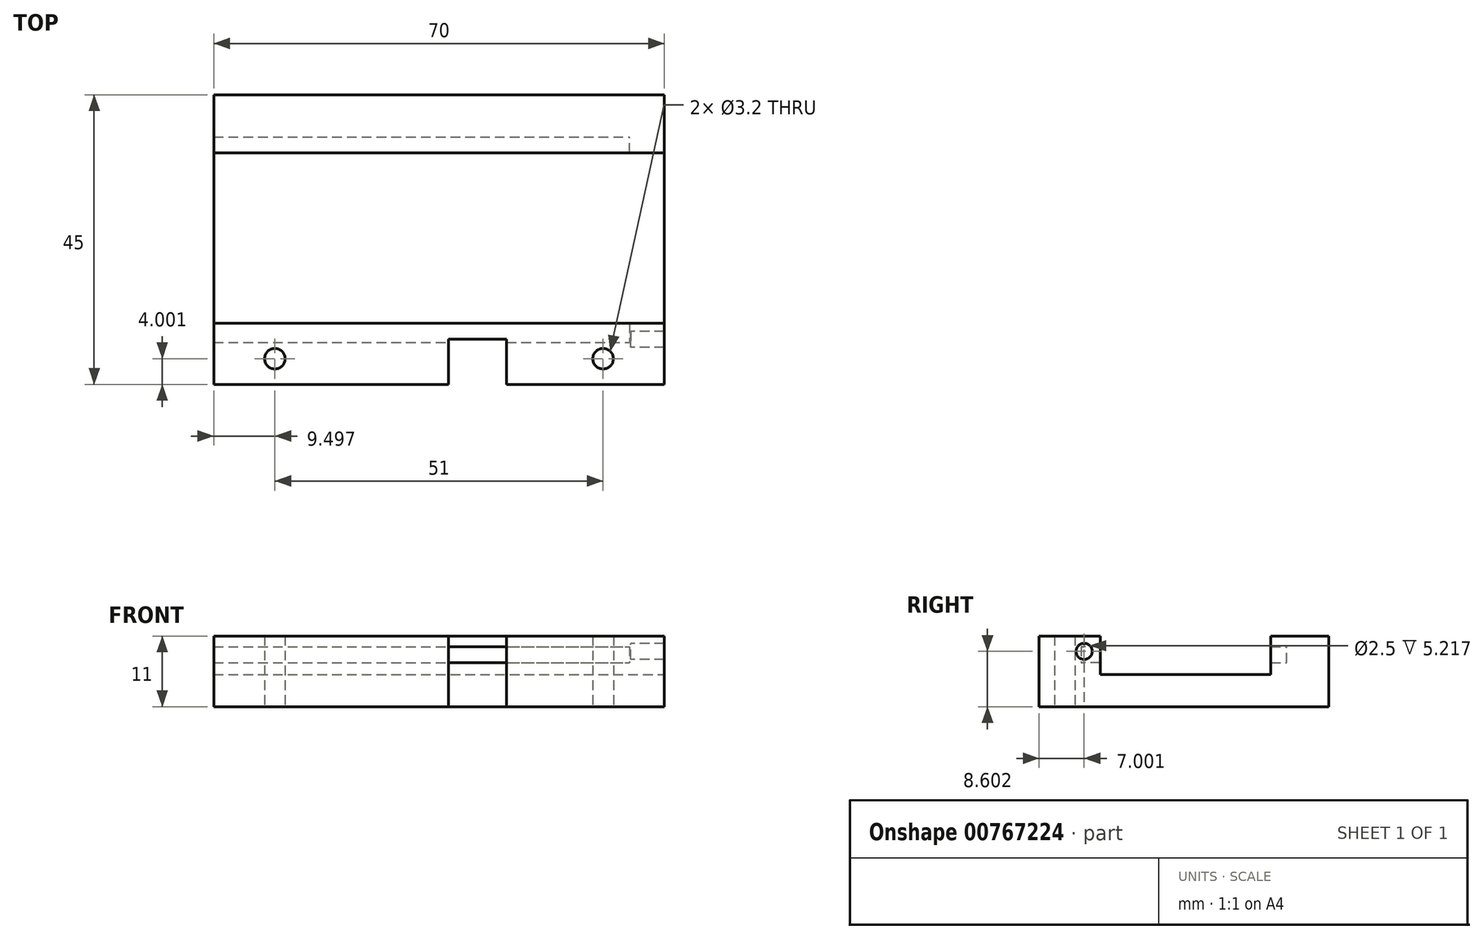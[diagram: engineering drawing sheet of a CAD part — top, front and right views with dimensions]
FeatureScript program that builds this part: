
annotation { "Feature Type Name" : "Feature", "Feature Type Description" : "" }
export const myFeature = defineFeature(function(context is Context, id is Id, definition is map)
    precondition{}
    {
        {
            var Q0;
            Q0=qCreatedBy(makeId("Top.planeOp"),FACE);
            var sketch = newSketch(context, id + "F0", { "sketchPlane" : qUnion([Q0])});
            skLineSegment(sketch, "E0.bottom", {"start": v(-36.38, 61.66) * mm, "end": v(33.62, 61.66) * mm});
            skLineSegment(sketch, "E0.top", {"start": v(-36.38, 16.66) * mm, "end": v(33.62, 16.66) * mm});
            skLineSegment(sketch, "E0.left", {"start": v(-36.38, 61.66) * mm, "end": v(-36.38, 16.66) * mm});
            skLineSegment(sketch, "E0.right", {"start": v(33.62, 61.66) * mm, "end": v(33.62, 16.66) * mm});
            skCircle(sketch, "E1", {"center": v(-26.88, 20.66) * mm, "radius": 1.6 * mm});
            skCircle(sketch, "E2", {"center": v(24.12, 20.66) * mm, "radius": 1.6 * mm});
            skLineSegment(sketch, "E3.bottom", {"start": v(-36.38, 52.66) * mm, "end": v(33.62, 52.66) * mm});
            skLineSegment(sketch, "E3.top", {"start": v(-36.38, 26.16) * mm, "end": v(33.62, 26.16) * mm});
            skLineSegment(sketch, "E3.left", {"start": v(-36.38, 52.66) * mm, "end": v(-36.38, 26.16) * mm});
            skLineSegment(sketch, "E3.right", {"start": v(33.62, 52.66) * mm, "end": v(33.62, 26.16) * mm});
            skLineSegment(sketch, "E4.bottom", {"start": v(0.12, 16.66) * mm, "end": v(9.12, 16.66) * mm});
            skLineSegment(sketch, "E4.top", {"start": v(0.12, 23.66) * mm, "end": v(9.12, 23.66) * mm});
            skLineSegment(sketch, "E4.left", {"start": v(0.12, 16.66) * mm, "end": v(0.12, 23.66) * mm});
            skLineSegment(sketch, "E4.right", {"start": v(9.12, 16.66) * mm, "end": v(9.12, 23.66) * mm});
            skSolve(sketch);
        }
        {
            var Q0;
            {var subQ1=sQuery(id+"F0.wireOp",EDGE,"E0.top");Q0=makeQuery(id+"F0.imprint","IMPRINT",FACE,{"disambiguationData":[TD([[makeQuery(id+"F0.imprint","IMPRINT",EDGE,{"derivedFrom":subQ1}),1.0]])]});}
            var Q1;
            {var subQ0=sQuery(id+"F0.wireOp",EDGE,"E0.bottom");Q1=makeQuery(id+"F0.imprint","IMPRINT",FACE,{"disambiguationData":[TD([[makeQuery(id+"F0.imprint","IMPRINT",EDGE,{"derivedFrom":subQ0}),-1.0]])]});}
            var Q2;
            {var subQ0=sQuery(id+"F0.wireOp",EDGE,"E3.bottom");Q2=makeQuery(id+"F0.imprint","IMPRINT",FACE,{"disambiguationData":[TD([[makeQuery(id+"F0.imprint","IMPRINT",EDGE,{"derivedFrom":subQ0}),-1.0]])]});}
            extrude(context, id + "F1", {"entities" : qUnion([Q0, Q1, Q2]), "depth" : 11 * mm, "offsetDistance" : 25 * mm});
        }
        {
            var Q0;
            {var subQ0=sQuery(id+"F0.wireOp",EDGE,"E3.bottom");Q0=makeQuery(id+"F0.imprint","IMPRINT",FACE,{"disambiguationData":[TD([[makeQuery(id+"F0.imprint","IMPRINT",EDGE,{"derivedFrom":subQ0}),-1.0]])]});}
            extrude(context, id + "F2", {"entities" : qUnion([Q0]), "operationType" : NewBodyOperationType.REMOVE, "depth" : 11 * mm, "offsetDistance" : 25 * mm, "hasSecondDirection" : true, "secondDirectionOppositeDirection" : false, "secondDirectionDepth" : 5 * mm});
        }
        {
            var Q0;
            {var subQ0=sQuery(id+"F0.wireOp",EDGE,"E0.bottom");Q0=makeQuery(id+"F0.imprint","IMPRINT",FACE,{"disambiguationData":[TD([[makeQuery(id+"F0.imprint","IMPRINT",EDGE,{"derivedFrom":subQ0}),-1.0]])]});}
            extrude(context, id + "F3", {"entities" : qUnion([Q0]), "operationType" : NewBodyOperationType.ADD, "depth" : 11 * mm, "offsetDistance" : 25 * mm});
        }
        {
            var Q0;
            Q0=qCreatedBy(makeId("Right.planeOp"),FACE);
            var sketch = newSketch(context, id + "F4", { "sketchPlane" : qUnion([Q0])});
            skLineSegment(sketch, "E5.bottom", {"start": v(52.64, 6.85) * mm, "end": v(55.14, 6.85) * mm});
            skLineSegment(sketch, "E5.top", {"start": v(52.64, 9.35) * mm, "end": v(55.14, 9.35) * mm});
            skLineSegment(sketch, "E5.left", {"start": v(52.64, 6.85) * mm, "end": v(52.64, 9.35) * mm});
            skLineSegment(sketch, "E5.right", {"start": v(55.14, 6.85) * mm, "end": v(55.14, 9.35) * mm});
            skLineSegment(sketch, "E6.bottom", {"start": v(28.18, 6.85) * mm, "end": v(23.18, 6.85) * mm});
            skLineSegment(sketch, "E6.top", {"start": v(28.18, 9.35) * mm, "end": v(23.18, 9.35) * mm});
            skLineSegment(sketch, "E6.left", {"start": v(28.18, 6.85) * mm, "end": v(28.18, 9.35) * mm});
            skLineSegment(sketch, "E6.right", {"start": v(23.18, 6.85) * mm, "end": v(23.18, 9.35) * mm});
            skSolve(sketch);
        }
        {
            var Q0;
            Q0=makeQuery(id+"F4.imprint","IMPRINT",FACE,{"disambiguationData":[TD([[makeQuery(id+"F4.imprint","IMPRINT",EDGE,{"derivedFrom":sQuery(id+"F4.wireOp",EDGE,"E5.bottom")}),1.0]])]});
            var Q1;
            Q1=makeQuery(id+"F4.imprint","IMPRINT",FACE,{"disambiguationData":[TD([[makeQuery(id+"F4.imprint","IMPRINT",EDGE,{"derivedFrom":sQuery(id+"F4.wireOp",EDGE,"E6.bottom")}),-1.0]])]});
            extrude(context, id + "F5", {"entities" : qUnion([Q0, Q1]), "operationType" : NewBodyOperationType.REMOVE, "oppositeDirection" : true, "depth" : 59.9 * mm, "offsetDistance" : 25 * mm, "hasSecondDirection" : true, "secondDirectionOppositeDirection" : false, "secondDirectionDepth" : 28.2 * mm});
        }
        {
            var Q0;
            Q0=qCreatedBy(makeId("Right.planeOp"),FACE);
            var sketch = newSketch(context, id + "F6", { "sketchPlane" : qUnion([Q0])});
            skCircle(sketch, "E7", {"center": v(23.66, 8.6) * mm, "radius": 1.25 * mm});
            skSolve(sketch);
        }
        {
            var Q0;
            Q0=makeQuery(id+"F6.imprint","IMPRINT",FACE,{"disambiguationData":[TD([[makeQuery(id+"F6.imprint","IMPRINT",EDGE,{"derivedFrom":sQuery(id+"F6.wireOp",EDGE,"E7")}),1.0]])]});
            extrude(context, id + "F7", {"entities" : qUnion([Q0]), "operationType" : NewBodyOperationType.REMOVE, "depth" : 49.1 * mm, "offsetDistance" : 25 * mm, "hasSecondDirection" : true, "secondDirectionOppositeDirection" : false, "secondDirectionDepth" : 28.4 * mm});
        }
    });
